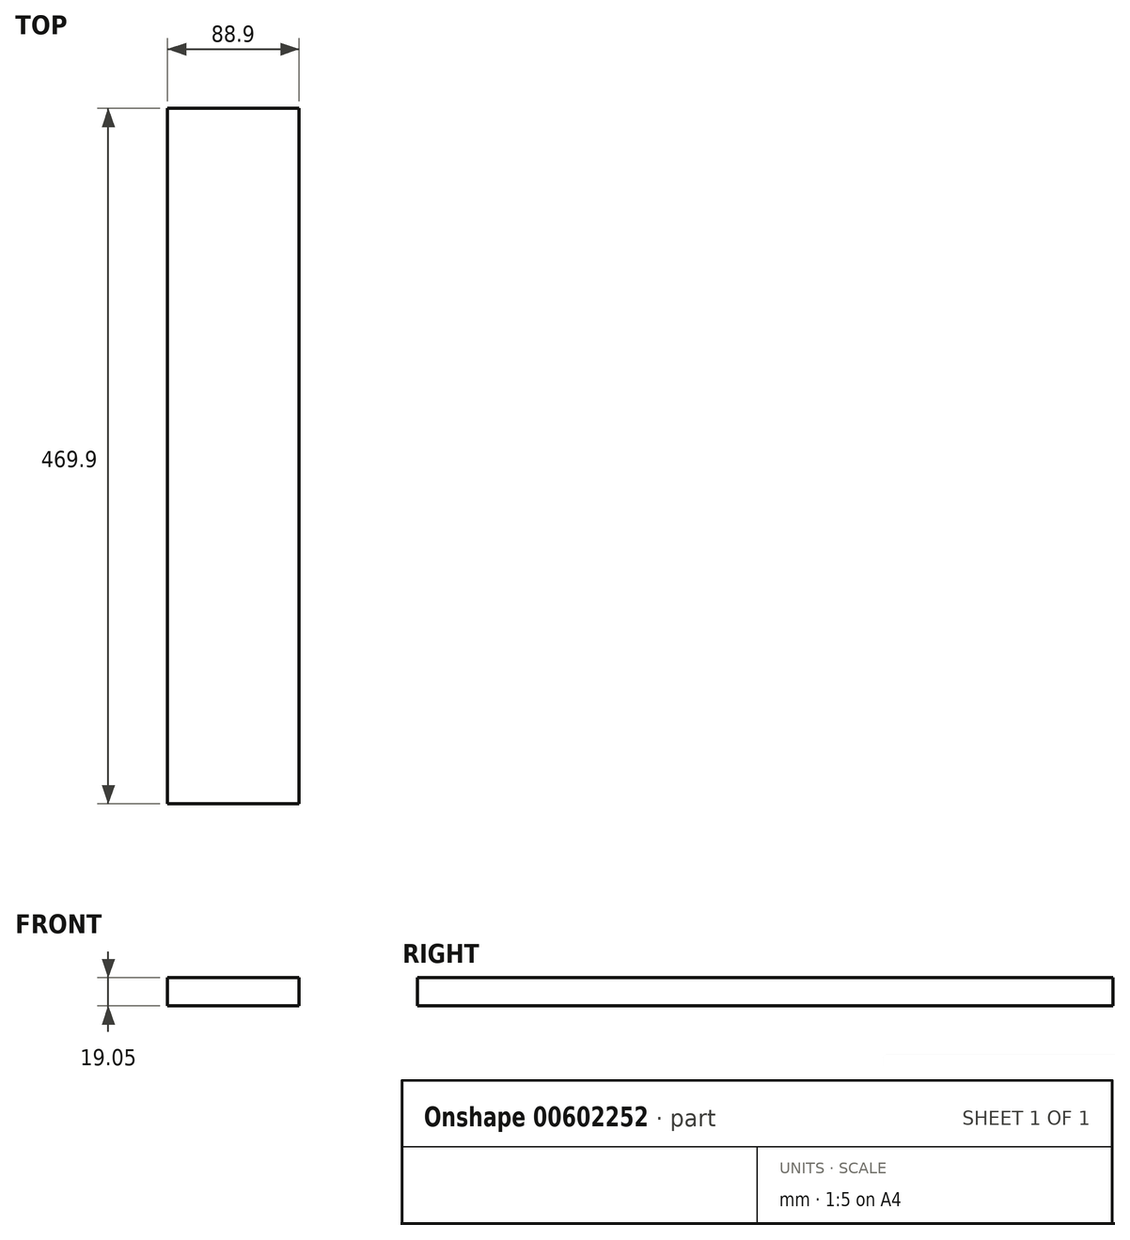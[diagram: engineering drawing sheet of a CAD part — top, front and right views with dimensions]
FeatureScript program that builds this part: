
annotation { "Feature Type Name" : "Feature", "Feature Type Description" : "" }
export const myFeature = defineFeature(function(context is Context, id is Id, definition is map)
    precondition{}
    {
        {
            var Q0;
            Q0=qCreatedBy(makeId("Front.planeOp"),FACE);
            var sketch = newSketch(context, id + "F0", { "sketchPlane" : qUnion([Q0]), "disableImprinting" : false});
            skLineSegment(sketch, "E0.bottom", {"start": v(0, 0) * mm, "end": v(88.9, 0) * mm});
            skLineSegment(sketch, "E0.top", {"start": v(0, 19.05) * mm, "end": v(88.9, 19.05) * mm});
            skLineSegment(sketch, "E0.left", {"start": v(0, 0) * mm, "end": v(0, 19.05) * mm});
            skLineSegment(sketch, "E0.right", {"start": v(88.9, 0) * mm, "end": v(88.9, 19.05) * mm});
            skSolve(sketch);
        }
        {
            var Q0;
            Q0 = qSketchRegion(id + "F0", true);
            extrude(context, id + "F1", {"entities" : qUnion([Q0]), "oppositeDirection" : true, "depth" : 469.9 * mm, "offsetDistance" : 25.4 * mm});
        }
    });
